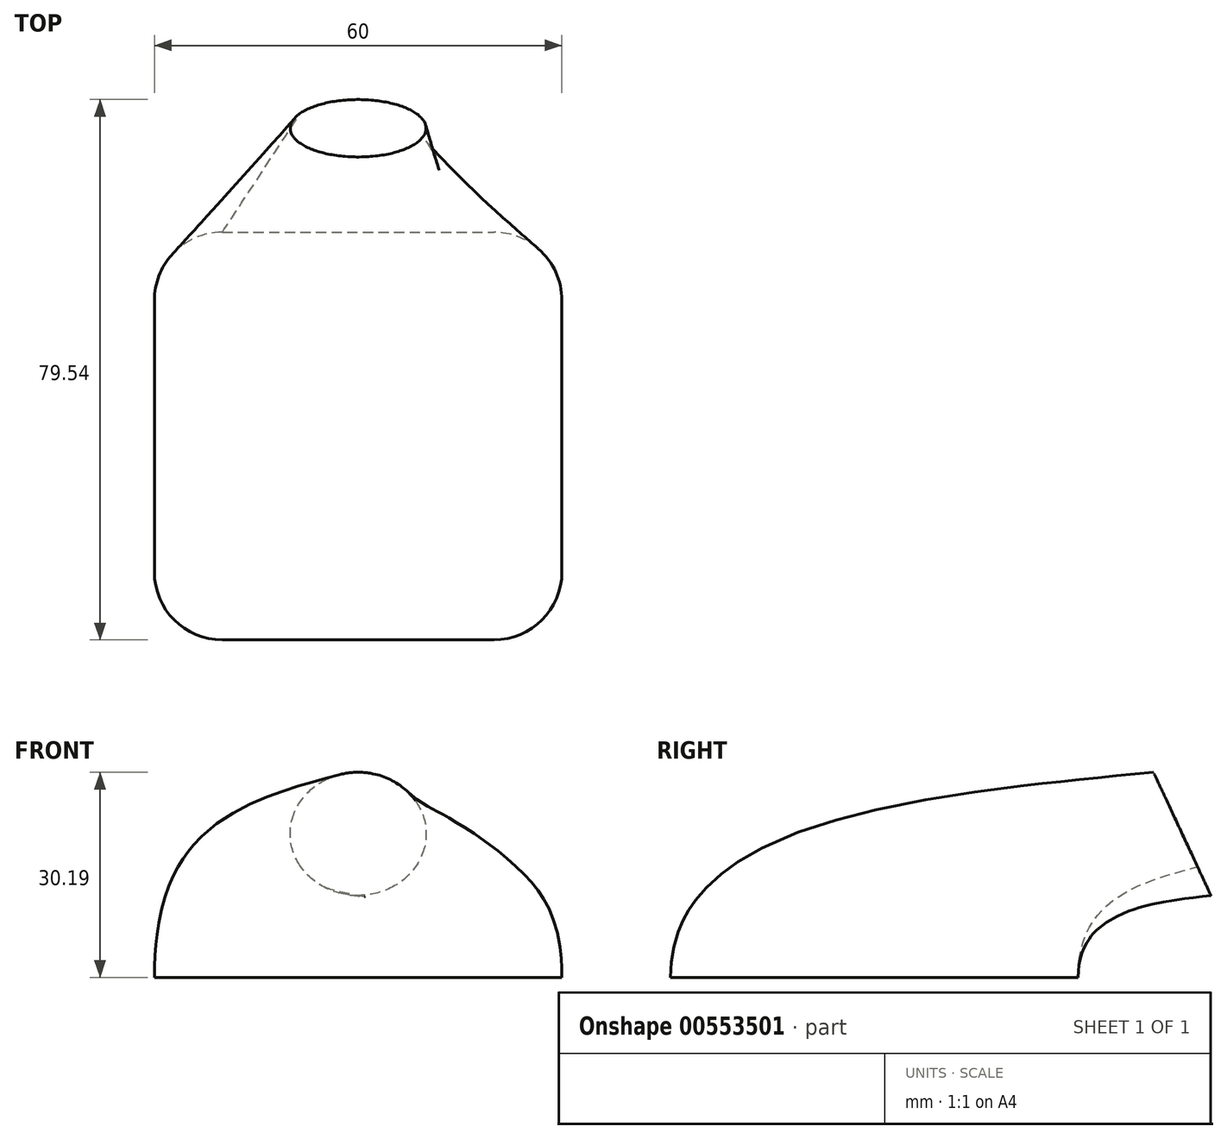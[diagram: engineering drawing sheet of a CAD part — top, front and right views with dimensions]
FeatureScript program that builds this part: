
annotation { "Feature Type Name" : "Feature", "Feature Type Description" : "" }
export const myFeature = defineFeature(function(context is Context, id is Id, definition is map)
    precondition{}
    {
        {
            var Q0;
            Q0=qCreatedBy(makeId("Top.planeOp"),FACE);
            var sketch = newSketch(context, id + "F0", { "sketchPlane" : qUnion([Q0])});
            skLineSegment(sketch, "E0.bottom", {"start": v(-20, 30) * mm, "end": v(20, 30) * mm});
            skLineSegment(sketch, "E0.top", {"start": v(-20, -30) * mm, "end": v(20, -30) * mm});
            skLineSegment(sketch, "E0.left", {"start": v(-30, 20) * mm, "end": v(-30, -20) * mm});
            skLineSegment(sketch, "E0.right", {"start": v(30, 20) * mm, "end": v(30, -20) * mm});
            skPoint(sketch, "E1.visualSharp", {"position": v(-30, 30) * mm});
            skArc(sketch, "E1.filletArc", {"start": v(-20, 30) * mm, "mid": v(-27.07, 27.07) * mm, "end": v(-30, 20) * mm});
            skPoint(sketch, "E2.visualSharp", {"position": v(30, 30) * mm});
            skArc(sketch, "E2.filletArc", {"start": v(30, 20) * mm, "mid": v(27.07, 27.07) * mm, "end": v(20, 30) * mm});
            skPoint(sketch, "E3.visualSharp", {"position": v(-30, -30) * mm});
            skArc(sketch, "E3.filletArc", {"start": v(-30, -20) * mm, "mid": v(-27.07, -27.07) * mm, "end": v(-20, -30) * mm});
            skPoint(sketch, "E4.visualSharp", {"position": v(30, -30) * mm});
            skArc(sketch, "E4.filletArc", {"start": v(20, -30) * mm, "mid": v(27.07, -27.07) * mm, "end": v(30, -20) * mm});
            skSolve(sketch);
        }
        {
            var Q0;
            Q0=qCreatedBy(makeId("Top.planeOp"),FACE);
            var sketch = newSketch(context, id + "F1", { "sketchPlane" : qUnion([Q0])});
            skLineSegment(sketch, "E5", {"start": v(-63.69, 0) * mm, "end": v(67.68, 0) * mm});
            skSolve(sketch);
        }
        {
            var Q0;
            Q0=sQuery(id+"F1.wireOp",EDGE,"E5");
            cPlane(context, id + "F2", {"entities" : qUnion([Q0]), "cplaneType" : CPlaneType.LINE_ANGLE, "offset" : 25 * mm, "angle" : 25 * degree, "width" : 150 * mm, "height" : 150 * mm});
        }
        {
            var Q0;
            Q0=qCreatedBy(id+"F2.planeOp",FACE);
            cPlane(context, id + "F3", {"entities" : qUnion([Q0]), "cplaneType" : CPlaneType.OFFSET, "offset" : 50 * mm, "width" : 150 * mm, "height" : 150 * mm});
        }
        {
            var Q0;
            Q0=qCreatedBy(id+"F3.planeOp",FACE);
            var sketch = newSketch(context, id + "F4", { "sketchPlane" : qUnion([Q0])});
            skCircle(sketch, "E6", {"center": v(0, 0) * mm, "radius": 10 * mm});
            skSolve(sketch);
        }
        {
            var Q0;
            Q0=makeQuery(id+"F0.imprint","IMPRINT",FACE,{"disambiguationData":[TD([[makeQuery(id+"F0.imprint","IMPRINT",EDGE,{"derivedFrom":sQuery(id+"F0.wireOp",EDGE,"E0.bottom")}),-1.0]])]});
            var Q1;
            Q1=makeQuery(id+"F4.imprint","IMPRINT",FACE,{"disambiguationData":[TD([[makeQuery(id+"F4.imprint","IMPRINT",EDGE,{"derivedFrom":sQuery(id+"F4.wireOp",EDGE,"E6")}),1.0]])]});
            loft(context, id + "F5", {"startCondition" : LoftEndDerivativeType.NORMAL_TO_PROFILE, "startMagnitude" : 2, "sheetProfilesArray" : [{ "sheetProfileEntities" : qUnion([Q0]) }, { "sheetProfileEntities" : qUnion([Q1]) }]});
        }
    });
